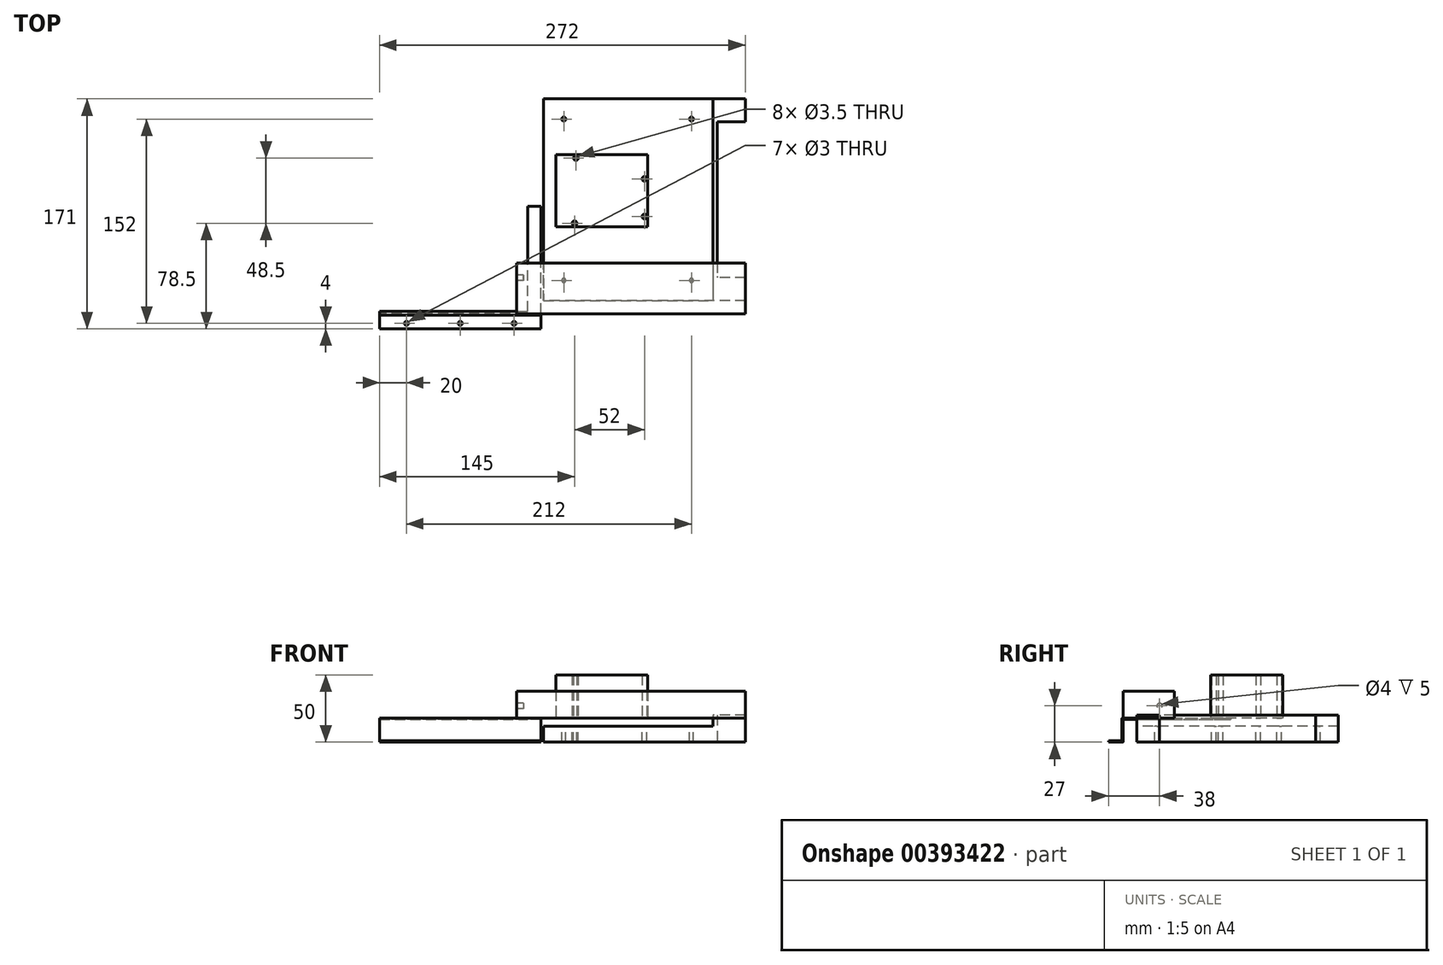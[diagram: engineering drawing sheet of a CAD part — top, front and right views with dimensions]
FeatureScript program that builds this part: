
annotation { "Feature Type Name" : "Feature", "Feature Type Description" : "" }
export const myFeature = defineFeature(function(context is Context, id is Id, definition is map)
    precondition{}
    {
        {
            var Q0;
            Q0=qCreatedBy(makeId("Top.planeOp"),FACE);
            var sketch = newSketch(context, id + "F0", { "sketchPlane" : qUnion([Q0])});
            skLineSegment(sketch, "E0.bottom", {"start": v(75, -75) * mm, "end": v(-75, -75) * mm});
            skLineSegment(sketch, "E0.top", {"start": v(75, 75) * mm, "end": v(-75, 75) * mm});
            skLineSegment(sketch, "E0.left", {"start": v(75, -75) * mm, "end": v(75, -58) * mm});
            skLineSegment(sketch, "E0.right", {"start": v(-75, -75) * mm, "end": v(-75, 75) * mm});
            skPoint(sketch, "E0.middle", {"position": v(0, 0) * mm});
            skLineSegment(sketch, "E1.bottom", {"start": v(75, 58) * mm, "end": v(54, 58) * mm});
            skLineSegment(sketch, "E1.top", {"start": v(75, -58) * mm, "end": v(54, -58) * mm});
            skLineSegment(sketch, "E1.right", {"start": v(54, 58) * mm, "end": v(54, -58) * mm});
            skLineSegment(sketch, "E2.trimOffspring", {"start": v(75, 58) * mm, "end": v(75, 75) * mm});
            skSolve(sketch);
        }
        {
            var Q0;
            Q0 = qSketchRegion(id + "F0", true);
            extrude(context, id + "F1", {"entities" : qUnion([Q0]), "depth" : 20 * mm});
        }
        {
            var Q0;
            Q0=makeQuery(id+"F1.opExtrude","CAP_FACE",FACE,{"disambiguationData":[OSD([sQuery(id+"F0.wireOp",EDGE,"E0.bottom"),sQuery(id+"F0.wireOp",EDGE,"E0.top"),sQuery(id+"F0.wireOp",EDGE,"E0.left"),sQuery(id+"F0.wireOp",EDGE,"E0.right")])],"isStart":false});
            var sketch = newSketch(context, id + "F2", { "sketchPlane" : qUnion([Q0])});
            skCircle(sketch, "E3", {"center": v(-60, 60) * mm, "radius": 1.5 * mm});
            skCircle(sketch, "E4", {"center": v(35, 60) * mm, "radius": 1.5 * mm});
            skCircle(sketch, "E5", {"center": v(-60, -60) * mm, "radius": 1.5 * mm});
            skCircle(sketch, "E6", {"center": v(35, -60) * mm, "radius": 1.5 * mm});
            skSolve(sketch);
        }
        {
            var Q0;
            Q0 = qSketchRegion(id + "F2", true);
            extrude(context, id + "F3", {"entities" : qUnion([Q0]), "operationType" : NewBodyOperationType.REMOVE, "oppositeDirection" : true, "depth" : 25 * mm});
        }
        {
            var Q0;
            Q0=makeQuery(id+"F1.opExtrude","SWEPT_FACE",FACE,{"disambiguationData":[OSD([sQuery(id+"F0.wireOp",EDGE,"E0.top")])]});
            cPlane(context, id + "F4", {"entities" : qUnion([Q0]), "cplaneType" : CPlaneType.OFFSET, "offset" : 40 * mm, "oppositeDirection" : true, "width" : 150 * mm, "height" : 150 * mm});
        }
        {
            var Q0;
            Q0=qCreatedBy(id+"F4.planeOp",FACE);
            var sketch = newSketch(context, id + "F5", { "sketchPlane" : qUnion([Q0])});
            skLineSegment(sketch, "E7.bottom", {"start": v(78, 18) * mm, "end": v(-3, 18) * mm});
            skLineSegment(sketch, "E7.top", {"start": v(77, 17) * mm, "end": v(-3, 17) * mm});
            skLineSegment(sketch, "E8.left", {"start": v(77, 17) * mm, "end": v(77, 0) * mm});
            skLineSegment(sketch, "E8.right", {"start": v(78, 18) * mm, "end": v(78, 1) * mm});
            skLineSegment(sketch, "E9.bottom", {"start": v(88, 0) * mm, "end": v(77, 0) * mm});
            skLineSegment(sketch, "E9.top", {"start": v(88, 1) * mm, "end": v(78, 1) * mm});
            skLineSegment(sketch, "E9.right", {"start": v(88, 0) * mm, "end": v(88, 1) * mm});
            skLineSegment(sketch, "E10", {"start": v(-3, 18) * mm, "end": v(-3, 17) * mm});
            skSolve(sketch);
        }
        {
            var Q0;
            Q0 = qSketchRegion(id + "F5", true);
            extrude(context, id + "F6", {"entities" : qUnion([Q0]), "oppositeDirection" : true, "depth" : 120 * mm});
        }
        {
            var Q0;
            Q0=makeQuery(id+"F6.opExtrude","SWEPT_EDGE",EDGE,{"disambiguationData":[OSD([sQuery(id+"F5.wireOp",EDGE,"E8.right"),sQuery(id+"F5.wireOp",EDGE,"E9.top")])]});
            var Q1;
            Q1=makeQuery(id+"F6.opExtrude","SWEPT_EDGE",EDGE,{"disambiguationData":[OSD([sQuery(id+"F5.wireOp",EDGE,"E8.left"),sQuery(id+"F5.wireOp",EDGE,"E9.bottom")])]});
            var Q2;
            Q2=makeQuery(id+"F6.opExtrude","SWEPT_EDGE",EDGE,{"disambiguationData":[OSD([sQuery(id+"F5.wireOp",EDGE,"E7.bottom"),sQuery(id+"F5.wireOp",EDGE,"E8.right")])]});
            var Q3;
            Q3=makeQuery(id+"F6.opExtrude","SWEPT_EDGE",EDGE,{"disambiguationData":[OSD([sQuery(id+"F5.wireOp",EDGE,"E7.top"),sQuery(id+"F5.wireOp",EDGE,"E8.left")])]});
            fillet(context, id + "F7", {"entities" : qUnion([Q0, Q1, Q2, Q3]), "radius" : 0.5 * mm, "tangentPropagation" : true, "allowEdgeOverflow" : false});
        }
        {
            var Q0;
            Q0=makeQuery(id+"F6.opExtrude","SWEPT_FACE",FACE,{"disambiguationData":[OSD([sQuery(id+"F5.wireOp",EDGE,"E9.top")])]});
            var sketch = newSketch(context, id + "F8", { "sketchPlane" : qUnion([Q0])});
            skCircle(sketch, "E11", {"center": v(-84, 15) * mm, "radius": 1.5 * mm});
            skCircle(sketch, "E12", {"center": v(-84, -25) * mm, "radius": 1.5 * mm});
            skCircle(sketch, "E13", {"center": v(-84, -65) * mm, "radius": 1.5 * mm});
            skSolve(sketch);
        }
        {
            var Q0;
            Q0 = qSketchRegion(id + "F8", true);
            extrude(context, id + "F9", {"entities" : qUnion([Q0]), "operationType" : NewBodyOperationType.REMOVE, "oppositeDirection" : true, "depth" : 25 * mm});
        }
        {
            var Q0;
            Q0=makeQuery(id+"F1.opExtrude","SWEPT_FACE",FACE,{"disambiguationData":[OSD([sQuery(id+"F0.wireOp",EDGE,"E0.bottom")])]});
            var sketch = newSketch(context, id + "F10", { "sketchPlane" : qUnion([Q0])});
            skLineSegment(sketch, "E14.bottom", {"start": v(-75, 20) * mm, "end": v(50.99, 20) * mm});
            skLineSegment(sketch, "E14.top", {"start": v(-75, 12) * mm, "end": v(50.99, 12) * mm});
            skLineSegment(sketch, "E14.left", {"start": v(-75, 20) * mm, "end": v(-75, 12) * mm});
            skLineSegment(sketch, "E14.right", {"start": v(50.99, 20) * mm, "end": v(50.99, 12) * mm});
            skSolve(sketch);
        }
        {
            var Q0;
            Q0 = qSketchRegion(id + "F10", true);
            extrude(context, id + "F11", {"entities" : qUnion([Q0]), "operationType" : NewBodyOperationType.REMOVE, "oppositeDirection" : true, "depth" : 166.4 * mm});
        }
        {
            var Q0;
            Q0=makeQuery(id+"F6.opExtrude","SWEPT_FACE",FACE,{"disambiguationData":[OSD([sQuery(id+"F5.wireOp",EDGE,"E7.bottom")])]});
            var sketch = newSketch(context, id + "F12", { "sketchPlane" : qUnion([Q0])});
            skLineSegment(sketch, "E15.bottom", {"start": v(75, -85) * mm, "end": v(-95, -85) * mm});
            skLineSegment(sketch, "E15.top", {"start": v(75, -47) * mm, "end": v(-95, -47) * mm});
            skLineSegment(sketch, "E15.left", {"start": v(75, -85) * mm, "end": v(75, -47) * mm});
            skLineSegment(sketch, "E15.right", {"start": v(-95, -85) * mm, "end": v(-95, -47) * mm});
            skPoint(sketch, "E15.middle", {"position": v(-10, -66) * mm});
            skSolve(sketch);
        }
        {
            var Q0;
            Q0 = qSketchRegion(id + "F12", true);
            extrude(context, id + "F13", {"entities" : qUnion([Q0]), "depth" : 20 * mm});
        }
        {
            var Q0;
            Q0=makeQuery(id+"F6.opExtrude","SWEPT_FACE",FACE,{"disambiguationData":[OSD([sQuery(id+"F5.wireOp",EDGE,"E7.bottom")])]});
            var sketch = newSketch(context, id + "F14", { "sketchPlane" : qUnion([Q0])});
            skCircle(sketch, "E16", {"center": v(-51, 31) * mm, "radius": 1.75 * mm});
            skCircle(sketch, "E17", {"center": v(-52, -17.5) * mm, "radius": 1.75 * mm});
            skCircle(sketch, "E18", {"center": v(0, -12.5) * mm, "radius": 1.75 * mm});
            skCircle(sketch, "E19", {"center": v(0, 15.5) * mm, "radius": 1.75 * mm});
            skLineSegment(sketch, "E20.bottom", {"start": v(-66, 33.5) * mm, "end": v(2.5, 33.5) * mm, "construction": true});
            skLineSegment(sketch, "E20.top", {"start": v(-66, -20) * mm, "end": v(2.5, -20) * mm, "construction": true});
            skLineSegment(sketch, "E20.left", {"start": v(-66, 33.5) * mm, "end": v(-66, -20) * mm, "construction": true});
            skLineSegment(sketch, "E20.right", {"start": v(2.5, 33.5) * mm, "end": v(2.5, -20) * mm, "construction": true});
            skSolve(sketch);
        }
        {
            var Q0;
            Q0 = qSketchRegion(id + "F14", true);
            extrude(context, id + "F15", {"entities" : qUnion([Q0]), "operationType" : NewBodyOperationType.REMOVE, "oppositeDirection" : true, "depth" : 25 * mm});
        }
        {
            var Q0;
            Q0=makeQuery(id+"F13.opExtrude","SWEPT_FACE",FACE,{"disambiguationData":[OSD([sQuery(id+"F12.wireOp",EDGE,"E15.right")])]});
            var sketch = newSketch(context, id + "F16", { "sketchPlane" : qUnion([Q0])});
            skCircle(sketch, "E21", {"center": v(58, 27) * mm, "radius": 2 * mm});
            skSolve(sketch);
        }
        {
            var Q0;
            Q0 = qSketchRegion(id + "F16", true);
            extrude(context, id + "F17", {"entities" : qUnion([Q0]), "operationType" : NewBodyOperationType.REMOVE, "oppositeDirection" : true, "depth" : 5 * mm});
        }
        {
            var Q0;
            Q0=makeQuery(id+"F6.opExtrude","SWEPT_FACE",FACE,{"disambiguationData":[OSD([sQuery(id+"F5.wireOp",EDGE,"E7.bottom")])]});
            var sketch = newSketch(context, id + "F18", { "sketchPlane" : qUnion([Q0])});
            skCircle(sketch, "E22", {"center": v(-51, 31) * mm, "radius": 1.75 * mm});
            skCircle(sketch, "E23", {"center": v(-52, -17.5) * mm, "radius": 1.75 * mm});
            skCircle(sketch, "E24", {"center": v(0, -12.5) * mm, "radius": 1.75 * mm});
            skCircle(sketch, "E25", {"center": v(0, 15.5) * mm, "radius": 1.75 * mm});
            skLineSegment(sketch, "E26.bottom", {"start": v(-66, 33.5) * mm, "end": v(2.5, 33.5) * mm});
            skLineSegment(sketch, "E26.top", {"start": v(-66, -20) * mm, "end": v(2.5, -20) * mm});
            skLineSegment(sketch, "E26.left", {"start": v(-66, 33.5) * mm, "end": v(-66, -20) * mm});
            skLineSegment(sketch, "E26.right", {"start": v(2.5, 33.5) * mm, "end": v(2.5, -20) * mm});
            skSolve(sketch);
        }
        {
            var Q0;
            Q0 = qSketchRegion(id + "F18", true);
            var Q1;
            Q1 = qConstructionFilter(qBodyType(qCreatedBy(id + "F18" ,EDGE), BodyType.WIRE), ConstructionObject.NO);
            extrude(context, id + "F19", {"entities" : qUnion([Q0]), "surfaceEntities" : qUnion([Q1]), "depth" : 32 * mm});
        }
        {
            var Q0;
            Q0=makeQuery(id+"F6.opExtrude","SWEPT_BODY",BODY,{"disambiguationData":[OSD([sQuery(id+"F5.wireOp",EDGE,"E7.bottom"),sQuery(id+"F5.wireOp",EDGE,"E7.top"),sQuery(id+"F5.wireOp",EDGE,"E8.left"),sQuery(id+"F5.wireOp",EDGE,"E8.right"),sQuery(id+"F5.wireOp",EDGE,"E9.bottom"),sQuery(id+"F5.wireOp",EDGE,"E9.top"),sQuery(id+"F5.wireOp",EDGE,"E9.right"),sQuery(id+"F5.wireOp",EDGE,"E10")])]});
            var Q1;
            Q1=makeQuery(id+"F6.opExtrude","CAP_EDGE",EDGE,{"disambiguationData":[OSD([sQuery(id+"F5.wireOp",EDGE,"E8.left")])],"isStart":false});
            transform(context, id + "F20", {"entities" : qUnion([Q0]), "transformType" : TransformType.ROTATION, "transformAxis" : qUnion([Q1]), "angle" : 90 * degree, "oppositeDirection" : true, "makeCopy" : false});
        }
    });
